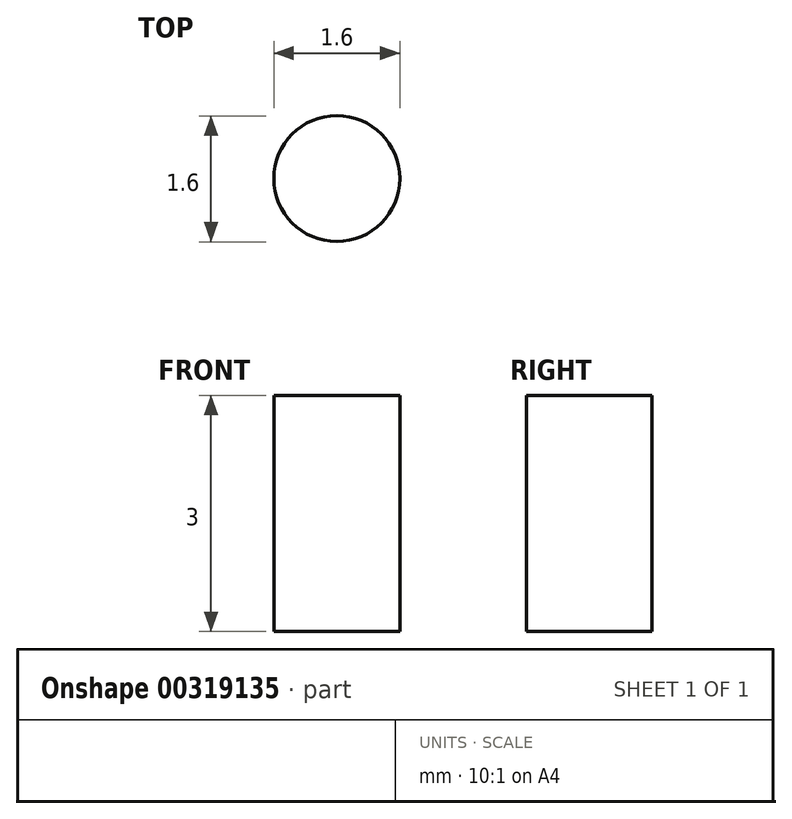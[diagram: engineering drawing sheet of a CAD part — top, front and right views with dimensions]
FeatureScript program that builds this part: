
annotation { "Feature Type Name" : "Feature", "Feature Type Description" : "" }
export const myFeature = defineFeature(function(context is Context, id is Id, definition is map)
    precondition{}
    {
        {
            var Q0;
            Q0=qCreatedBy(makeId("Top.planeOp"),FACE);
            var sketch = newSketch(context, id + "F0", { "sketchPlane" : qUnion([Q0])});
            skLineSegment(sketch, "E0", {"start": v(16.05, -42.01) * mm, "end": v(16.05, 51.5) * mm});
            skLineSegment(sketch, "E1", {"start": v(16.05, 51.5) * mm, "end": v(-3.92, 53.28) * mm});
            skLineSegment(sketch, "E2", {"start": v(-3.92, 53.28) * mm, "end": v(-22.3, 47.75) * mm});
            skFitSpline(sketch, "E3", {"points": [v(-22.3, 47.75) * mm, v(-26.52, 39.28) * mm, v(-25.73, 31.23) * mm, v(-20.85, 24.9) * mm], "startDerivative": vector(-15.1, -23.53) * mm, "endDerivative": vector(17.54, -18.18) * mm});
            skLineSegment(sketch, "E4", {"start": v(-20.85, 24.9) * mm, "end": v(-2.64, 24.9) * mm});
            skLineSegment(sketch, "E5", {"start": v(-2.64, 24.9) * mm, "end": v(-2.64, 17.9) * mm});
            skLineSegment(sketch, "E6", {"start": v(-2.64, 17.9) * mm, "end": v(-10.16, 17.9) * mm});
            skFitSpline(sketch, "E7", {"points": [v(-10.16, 17.9) * mm, v(-11.56, 16.8) * mm, v(-11.56, 15.36) * mm, v(-10.16, 14.47) * mm, v(-5.13, 11.58) * mm, v(-1.35, 7.7) * mm, v(0, 0) * mm], "startDerivative": vector(-14.55, -7.72) * mm, "endDerivative": vector(2.4, -34.65) * mm});
            skLineSegment(sketch, "E8", {"start": v(0, 0) * mm, "end": v(0, -41.26) * mm});
            skFitSpline(sketch, "E9", {"points": [v(0, -41.26) * mm, v(3.56, -44.59) * mm, v(8.63, -46.08) * mm, v(13.2, -44.84) * mm, v(16.05, -42.01) * mm], "startDerivative": vector(12.7, -14.4) * mm, "endDerivative": vector(10.97, 13.55) * mm});
            skEllipse(sketch, "E10", {"center": v(8.12, -37.52) * mm, "majorRadius": 3.49 * mm, "minorRadius": 2.66 * mm, "majorAxis": v(0, -1)});
            skLineSegment(sketch, "E11", {"start": v(-31.82, 8.8) * mm, "end": v(-31.92, 65.12) * mm});
            skLineSegment(sketch, "E12", {"start": v(-31.92, 65.12) * mm, "end": v(-12.3, 65.12) * mm});
            skLineSegment(sketch, "E13", {"start": v(-12.3, 65.12) * mm, "end": v(-12.3, 70.3) * mm});
            skFitSpline(sketch, "E14", {"points": [v(-12.3, 70.3) * mm, v(-14.66, 74.07) * mm, v(-18.59, 76.26) * mm, v(-23.76, 78.62) * mm, v(-29.26, 79.4) * mm, v(-34.28, 78.62) * mm, v(-38.51, 76.1) * mm, v(-41.18, 72.34) * mm, v(-42.75, 67.48) * mm, v(-42.9, 63.71) * mm], "startDerivative": vector(-18.6, 39.45) * mm, "endDerivative": vector(0.9, -36.97) * mm});
            skLineSegment(sketch, "E15", {"start": v(-42.9, 63.71) * mm, "end": v(-42.9, 8.8) * mm});
            skLineSegment(sketch, "E16", {"start": v(-42.9, 8.8) * mm, "end": v(-31.82, 8.8) * mm});
            skCircle(sketch, "E17", {"center": v(-31.83, 13.63) * mm, "radius": 0.8 * mm});
            skLineSegment(sketch, "E18", {"start": v(-32.72, 14.45) * mm, "end": v(-30.46, 14.45) * mm, "construction": true});
            skCircle(sketch, "E19.MirrorC", {"center": v(-31.83, 15.27) * mm, "radius": 0.8 * mm});
            skLineSegment(sketch, "E20", {"start": v(-32.72, 16) * mm, "end": v(-30.86, 16) * mm, "construction": true});
            skSolve(sketch);
        }
        {
            var Q0;
            {var subQ0=sQuery(id+"F0.wireOp",EDGE,"E17");var subQ1=sQuery(id+"F0.wireOp",EDGE,"E11");var subQ2=makeQuery(id+"F0.imprint","INTERSECT",VERTEX,{"disambiguationData":[OD(0.0)],"derivedFrom":[subQ1,subQ0]});Q0=makeQuery(id+"F0.imprint","IMPRINT",FACE,{"disambiguationData":[TD([[makeQuery(id+"F0.imprint","IMPRINT",EDGE,{"disambiguationData":[TD([[subQ2,-1.0]])],"derivedFrom":subQ1}),1.0]])]});}
            var Q1;
            {var subQ0=sQuery(id+"F0.wireOp",EDGE,"E17");var subQ1=sQuery(id+"F0.wireOp",EDGE,"E11");var subQ2=makeQuery(id+"F0.imprint","INTERSECT",VERTEX,{"disambiguationData":[OD(0.0)],"derivedFrom":[subQ1,subQ0]});Q1=makeQuery(id+"F0.imprint","IMPRINT",FACE,{"disambiguationData":[TD([[makeQuery(id+"F0.imprint","IMPRINT",EDGE,{"disambiguationData":[TD([[subQ2,-1.0]])],"derivedFrom":subQ1}),-1.0]])]});}
            extrude(context, id + "F1", {"entities" : qUnion([Q0, Q1]), "depth" : 3 * mm});
        }
        {
            var Q0;
            Q0=sQuery(id+"F0.wireOp",EDGE,"E11");
            extrude(context, id + "F2", {"bodyType" : ToolBodyType.SURFACE, "surfaceEntities" : qUnion([Q0]), "depth" : 3 * mm});
        }
    });
